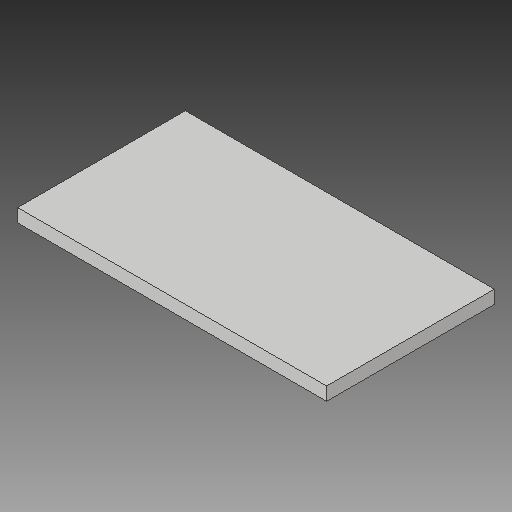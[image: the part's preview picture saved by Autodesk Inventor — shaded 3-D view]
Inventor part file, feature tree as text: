
AUTODESK INVENTOR PART (.ipt)
format: ipt  version: 2017 (Build 210142000, 142)  size: 89,088 bytes
history: native  units: in
note: dims shown in document units (in); Inventor stores cm internally (conversion verified against a paired STEP export)
features: extrude x1, sketch x1
ambient origin geometry x8: Origin, YZ Plane, XZ Plane, XY Plane, X Axis, Y Axis, Z Axis, Center Point
bodies: Solid1 (feature_tree)
feature tree (2):
  extrude  "Extrusion1"  Depth=9.5in
  sketch  "Sketch1"  dims[d0=17.5in d1=9.5in d2=0.75in d3=0.0in]
